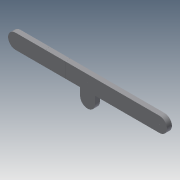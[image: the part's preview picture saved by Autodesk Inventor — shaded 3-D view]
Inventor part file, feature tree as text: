
AUTODESK INVENTOR PART (.ipt)
format: ipt  version: 2013 (Build 170138000, 138)  size: 128,000 bytes
history: native  units: mm
features: extrude x4, sketch x4
ambient origin geometry x8: Origin, YZ Plane, XZ Plane, XY Plane, X Axis, Y Axis, Z Axis, Center Point
bodies: Solid1 (feature_tree)
feature tree (8):
  extrude  "Extrusion1"  Depth=6.0mm
  extrude  "Extrusion2"  Depth=12.0mm
  extrude  "Extrusion3"  Depth=12.0mm
  extrude  "Extrusion4"  Depth=0.01mm
  sketch  "Sketch1"  dims[d17=18.0mm d18=6.0mm]
  sketch  "Sketch2"  dims[d19=8.0mm d20=12.0mm]
  sketch  "Sketch3"  dims[d21=8.0mm d22=12.0mm]
  sketch  "Sketch4"  dims[d23=0.01mm d24=0.01mm d25=0.01mm d26=0.01mm d27=3.0mm d28=2.0mm d29=0.0mm d30=0.1mm d31=0.1mm d32=2.0mm d33=0.0mm d34=0.1mm d35=2.0mm d36=0.0mm d37=0.1mm d38=2.0mm d39=0.0mm]
